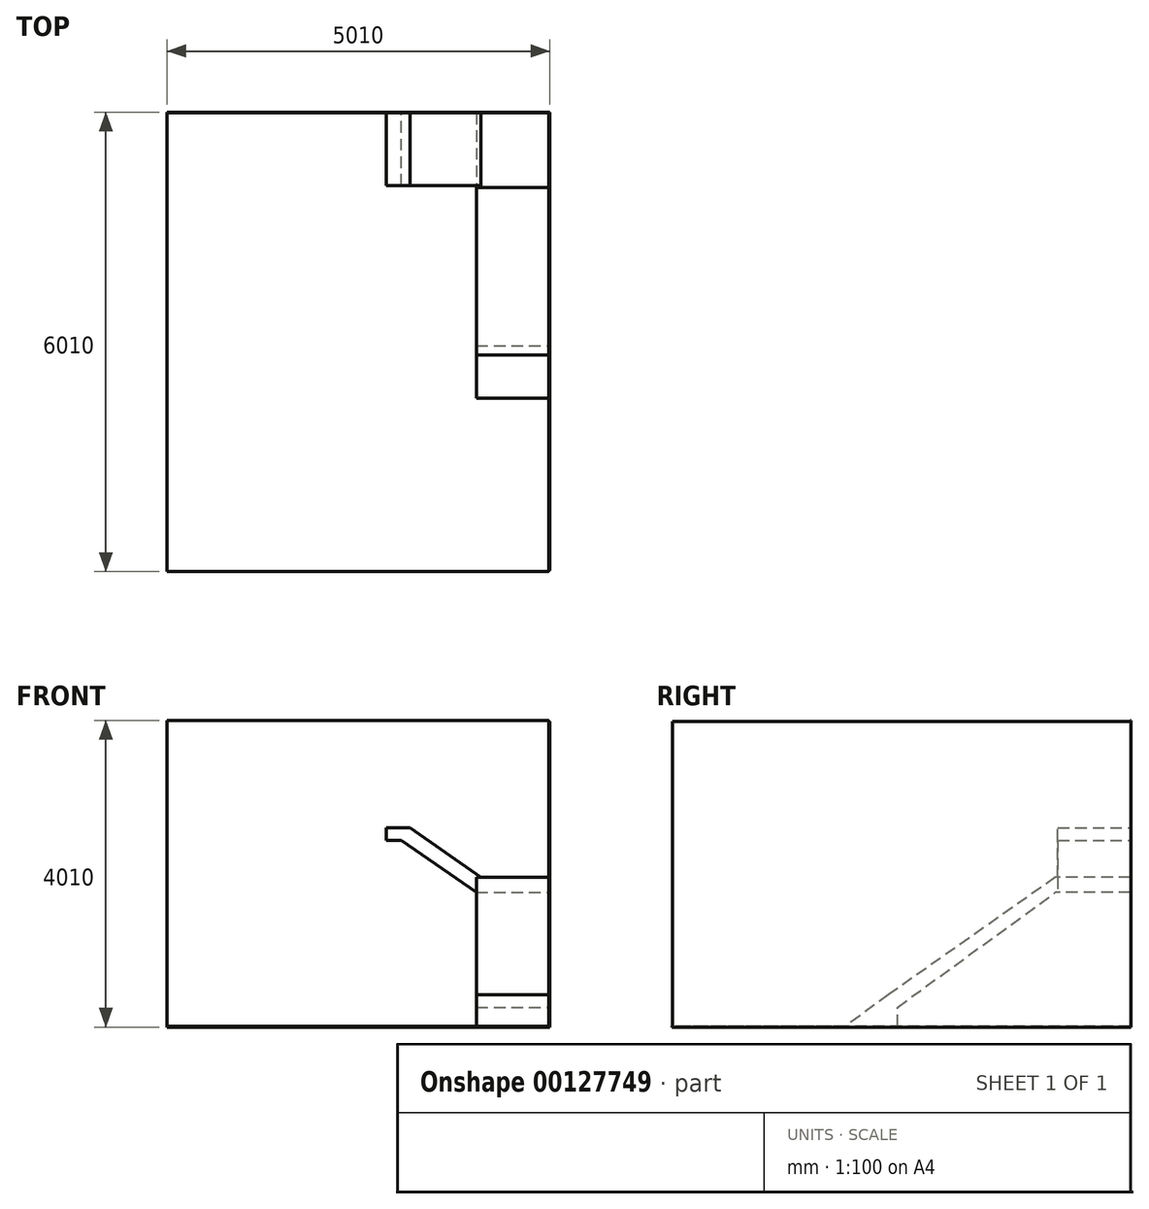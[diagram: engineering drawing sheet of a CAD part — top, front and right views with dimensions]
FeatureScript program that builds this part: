
annotation { "Feature Type Name" : "Feature", "Feature Type Description" : "" }
export const myFeature = defineFeature(function(context is Context, id is Id, definition is map)
    precondition{}
    {
        {
            var Q0;
            Q0=qCreatedBy(makeId("Top.planeOp"),FACE);
            var sketch = newSketch(context, id + "F0", { "sketchPlane" : qUnion([Q0])});
            skLineSegment(sketch, "E0.bottom", {"start": v(0, 0) * mm, "end": v(-5000, 0) * mm});
            skLineSegment(sketch, "E0.top", {"start": v(0, -6000) * mm, "end": v(-5000, -6000) * mm});
            skLineSegment(sketch, "E0.left", {"start": v(0, 0) * mm, "end": v(0, -6000) * mm});
            skLineSegment(sketch, "E0.right", {"start": v(-5000, 0) * mm, "end": v(-5000, -6000) * mm});
            skSolve(sketch);
        }
        {
            var Q0;
            Q0=makeQuery(id+"F0.imprint","IMPRINT",FACE,{"disambiguationData":[TD([[makeQuery(id+"F0.imprint","IMPRINT",EDGE,{"derivedFrom":sQuery(id+"F0.wireOp",EDGE,"E0.bottom")}),1.0]])]});
            extrude(context, id + "F1", {"entities" : qUnion([Q0]), "oppositeDirection" : true, "depth" : 10 * mm});
        }
        {
            var Q0;
            Q0=qCreatedBy(makeId("Front.planeOp"),FACE);
            var sketch = newSketch(context, id + "F2", { "sketchPlane" : qUnion([Q0])});
            skLineSegment(sketch, "E1.bottom", {"start": v(0, 0) * mm, "end": v(-5000, 0) * mm});
            skLineSegment(sketch, "E1.top", {"start": v(0, -10) * mm, "end": v(-5000, -10) * mm});
            skLineSegment(sketch, "E1.left", {"start": v(0, 0) * mm, "end": v(0, -10) * mm});
            skLineSegment(sketch, "E1.right", {"start": v(-5000, 0) * mm, "end": v(-5000, -10) * mm});
            skLineSegment(sketch, "E2.top", {"start": v(0, 4000) * mm, "end": v(-5000, 4000) * mm});
            skLineSegment(sketch, "E2.left", {"start": v(0, 0) * mm, "end": v(0, 4000) * mm});
            skLineSegment(sketch, "E2.right", {"start": v(-5000, 0) * mm, "end": v(-5000, 4000) * mm});
            skLineSegment(sketch, "E3", {"start": v(0, 0) * mm, "end": v(0, 1750) * mm, "construction": true});
            skLineSegment(sketch, "E4", {"start": v(0, 1750) * mm, "end": v(-950, 1750) * mm, "construction": true});
            skLineSegment(sketch, "E5", {"start": v(-950, 1750) * mm, "end": v(-1930, 1750) * mm, "construction": true});
            skLineSegment(sketch, "E6.bottom", {"start": v(-1930, 1750) * mm, "end": v(-950, 1750) * mm, "construction": true});
            skLineSegment(sketch, "E6.top", {"start": v(-1930, 0) * mm, "end": v(-950, 0) * mm, "construction": true});
            skLineSegment(sketch, "E6.left", {"start": v(-1930, 1750) * mm, "end": v(-1930, 0) * mm, "construction": true});
            skLineSegment(sketch, "E6.right", {"start": v(-950, 1750) * mm, "end": v(-950, 0) * mm, "construction": true});
            skLineSegment(sketch, "E7", {"start": v(-1930, 0) * mm, "end": v(-1930, 2430) * mm, "construction": true});
            skLineSegment(sketch, "E8", {"start": v(-1930, 2430) * mm, "end": v(-950, 1750) * mm});
            skLineSegment(sketch, "E9", {"start": v(-1930, 2430) * mm, "end": v(-2130, 2430) * mm});
            skLineSegment(sketch, "E10", {"start": v(-1930, 2430) * mm, "end": v(-1815.98, 2594.32) * mm});
            skLineSegment(sketch, "E11", {"start": v(-950, 1750) * mm, "end": v(-854.02, 1925.46) * mm});
            skLineSegment(sketch, "E12", {"start": v(-854.02, 1925.46) * mm, "end": v(-1815.98, 2594.32) * mm});
            skLineSegment(sketch, "E13", {"start": v(-2130, 2430) * mm, "end": v(-2130, 2594.32) * mm});
            skLineSegment(sketch, "E14", {"start": v(-2130, 2594.32) * mm, "end": v(-1815.98, 2594.32) * mm});
            skLineSegment(sketch, "E15", {"start": v(-2130, 2594.32) * mm, "end": v(-5000, 2594.32) * mm});
            skLineSegment(sketch, "E16.bottom", {"start": v(-5000, 2594.32) * mm, "end": v(-1815.98, 2594.32) * mm});
            skLineSegment(sketch, "E16.top", {"start": v(-5000, 2604.32) * mm, "end": v(-1815.98, 2604.32) * mm});
            skLineSegment(sketch, "E16.left", {"start": v(-5000, 2594.32) * mm, "end": v(-5000, 2604.32) * mm});
            skLineSegment(sketch, "E16.right", {"start": v(-1815.98, 2594.32) * mm, "end": v(-1815.98, 2604.32) * mm});
            skSolve(sketch);
        }
        {
            var Q0;
            Q0=makeQuery(id+"F2.imprint","IMPRINT",FACE,{"disambiguationData":[TD([[makeQuery(id+"F2.imprint","IMPRINT",EDGE,{"derivedFrom":sQuery(id+"F2.wireOp",EDGE,"E1.bottom")}),-1.0]])]});
            var Q1;
            Q1=makeQuery(id+"F2.imprint","IMPRINT",FACE,{"disambiguationData":[TD([[makeQuery(id+"F2.imprint","IMPRINT",EDGE,{"derivedFrom":sQuery(id+"F2.wireOp",EDGE,"E1.top")}),-1.0]])]});
            var Q2;
            Q2=makeQuery(id+"F2.imprint","IMPRINT",FACE,{"disambiguationData":[TD([[makeQuery(id+"F2.imprint","IMPRINT",EDGE,{"derivedFrom":sQuery(id+"F2.wireOp",EDGE,"E8")}),1.0]])]});
            var Q3;
            Q3=makeQuery(id+"F2.imprint","IMPRINT",FACE,{"disambiguationData":[TD([[makeQuery(id+"F2.imprint","IMPRINT",EDGE,{"derivedFrom":sQuery(id+"F2.wireOp",EDGE,"E9")}),-1.0]])]});
            var Q4;
            Q4=makeQuery(id+"F2.imprint","IMPRINT",FACE,{"disambiguationData":[TD([[makeQuery(id+"F2.imprint","IMPRINT",EDGE,{"derivedFrom":sQuery(id+"F2.wireOp",EDGE,"E16.top")}),-1.0]])]});
            extrude(context, id + "F3", {"entities" : qUnion([Q0, Q1, Q2, Q3, Q4]), "operationType" : NewBodyOperationType.ADD, "oppositeDirection" : true, "depth" : 10 * mm});
        }
        {
            var Q0;
            Q0=qCreatedBy(makeId("Right.planeOp"),FACE);
            var sketch = newSketch(context, id + "F4", { "sketchPlane" : qUnion([Q0])});
            skLineSegment(sketch, "E17.bottom", {"start": v(0, 0) * mm, "end": v(-980, 0) * mm});
            skLineSegment(sketch, "E17.top", {"start": v(0, 1750) * mm, "end": v(-980, 1750) * mm});
            skLineSegment(sketch, "E17.left", {"start": v(0, 0) * mm, "end": v(0, 1750) * mm});
            skLineSegment(sketch, "E18", {"start": v(0, 1750) * mm, "end": v(-3140, 1750) * mm, "construction": true});
            skLineSegment(sketch, "E19", {"start": v(-3048.34, 0) * mm, "end": v(-3048.34, 250) * mm});
            skLineSegment(sketch, "E20", {"start": v(-3048.34, 250) * mm, "end": v(-980, 1750) * mm});
            skLineSegment(sketch, "E21", {"start": v(0, 1750) * mm, "end": v(0, 1950) * mm});
            skLineSegment(sketch, "E22", {"start": v(0, 1950) * mm, "end": v(-980, 1950) * mm});
            skLineSegment(sketch, "E23", {"start": v(-3048.34, 250) * mm, "end": v(-3165.75, 411.9) * mm, "construction": true});
            skLineSegment(sketch, "E24", {"start": v(-980, 1950) * mm, "end": v(-3165.75, 411.9) * mm});
            skLineSegment(sketch, "E25", {"start": v(-3165.75, 411.9) * mm, "end": v(-3733.73, 0) * mm});
            skLineSegment(sketch, "E26", {"start": v(-3733.73, 0) * mm, "end": v(-3048.34, 0) * mm});
            skLineSegment(sketch, "E27.bottom", {"start": v(0, 0) * mm, "end": v(10, 0) * mm, "construction": true});
            skLineSegment(sketch, "E27.top", {"start": v(0, -10) * mm, "end": v(10, -10) * mm, "construction": true});
            skLineSegment(sketch, "E27.left", {"start": v(0, 0) * mm, "end": v(0, -10) * mm, "construction": true});
            skLineSegment(sketch, "E27.right", {"start": v(10, 0) * mm, "end": v(10, -10) * mm, "construction": true});
            skLineSegment(sketch, "E28.bottom", {"start": v(10, -10) * mm, "end": v(-5990, -10) * mm});
            skLineSegment(sketch, "E28.top", {"start": v(10, 3990) * mm, "end": v(-5990, 3990) * mm});
            skLineSegment(sketch, "E28.left", {"start": v(10, -10) * mm, "end": v(10, 3990) * mm});
            skLineSegment(sketch, "E28.right", {"start": v(-5990, -10) * mm, "end": v(-5990, 3990) * mm});
            skSolve(sketch);
        }
        {
            var Q0;
            Q0=makeQuery(id+"F4.imprint","IMPRINT",FACE,{"disambiguationData":[TD([[makeQuery(id+"F4.imprint","IMPRINT",EDGE,{"derivedFrom":sQuery(id+"F4.wireOp",EDGE,"E17.top")}),1.0]])]});
            var Q1;
            Q1=makeQuery(id+"F4.imprint","IMPRINT",FACE,{"disambiguationData":[TD([[makeQuery(id+"F4.imprint","IMPRINT",EDGE,{"derivedFrom":sQuery(id+"F4.wireOp",EDGE,"E17.top")}),-1.0]])]});
            extrude(context, id + "F5", {"entities" : qUnion([Q0, Q1]), "operationType" : NewBodyOperationType.ADD, "depth" : 10 * mm});
        }
        {
            var Q0;
            Q0=makeQuery(id+"F4.imprint","IMPRINT",FACE,{"disambiguationData":[TD([[makeQuery(id+"F4.imprint","IMPRINT",EDGE,{"derivedFrom":sQuery(id+"F4.wireOp",EDGE,"E17.top")}),-1.0]])]});
            extrude(context, id + "F6", {"entities" : qUnion([Q0]), "operationType" : NewBodyOperationType.ADD, "oppositeDirection" : true, "depth" : 950 * mm});
        }
        {
            var Q0;
            Q0=makeQuery(id+"F2.imprint","IMPRINT",FACE,{"disambiguationData":[TD([[makeQuery(id+"F2.imprint","IMPRINT",EDGE,{"derivedFrom":sQuery(id+"F2.wireOp",EDGE,"E8")}),1.0]])]});
            var Q1;
            Q1=makeQuery(id+"F2.imprint","IMPRINT",FACE,{"disambiguationData":[TD([[makeQuery(id+"F2.imprint","IMPRINT",EDGE,{"derivedFrom":sQuery(id+"F2.wireOp",EDGE,"E9")}),-1.0]])]});
            extrude(context, id + "F7", {"entities" : qUnion([Q0, Q1]), "operationType" : NewBodyOperationType.ADD, "depth" : 950 * mm});
        }
    });
